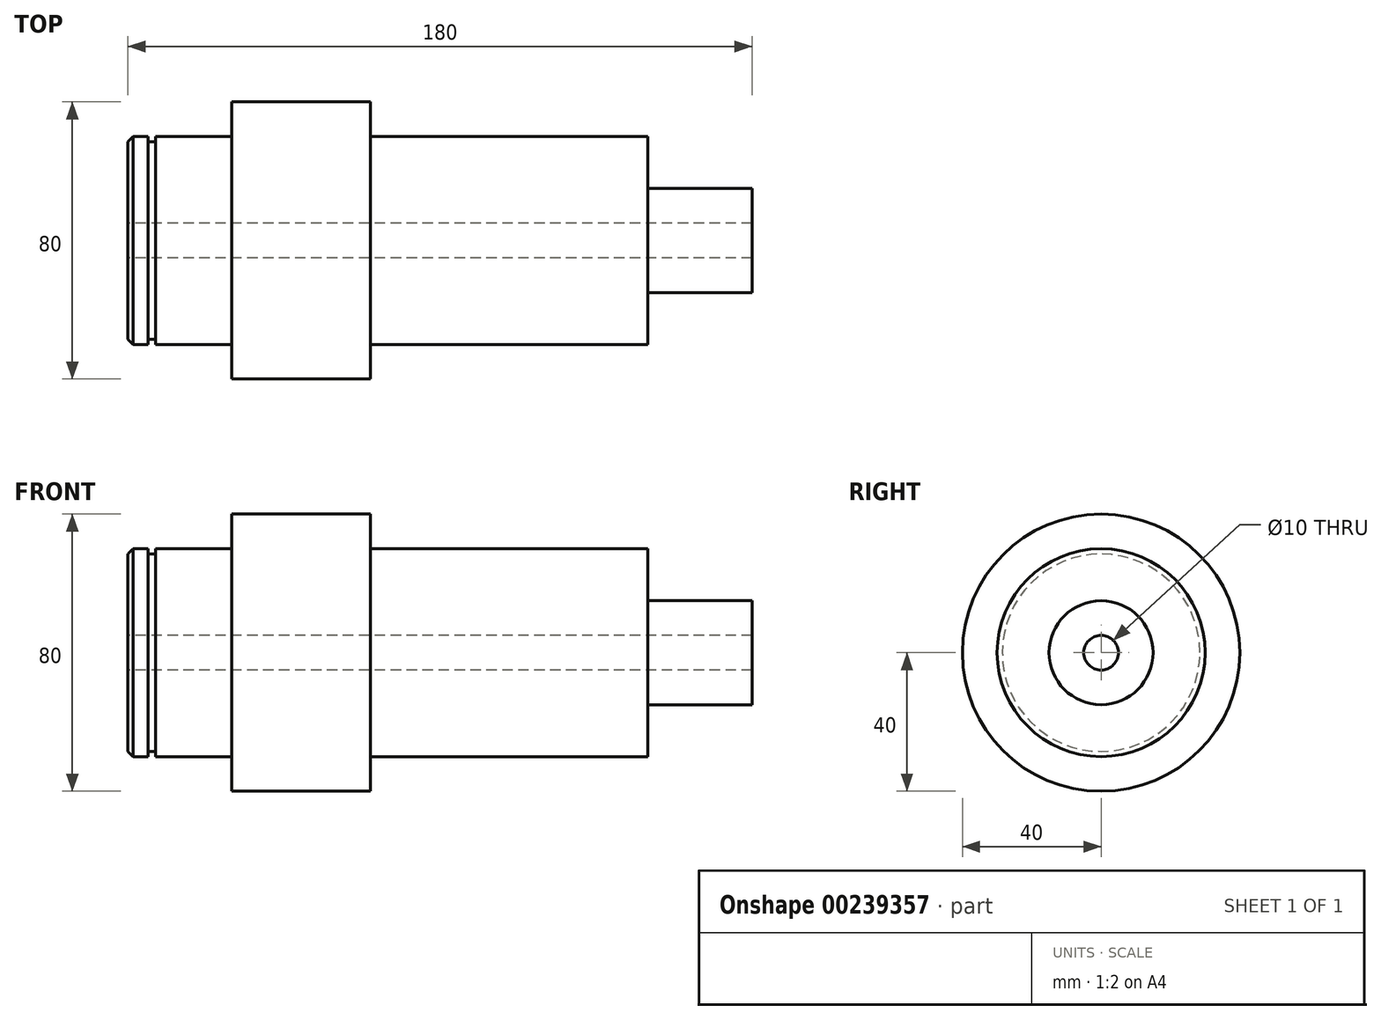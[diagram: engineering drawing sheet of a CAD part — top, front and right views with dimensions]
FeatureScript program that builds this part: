
annotation { "Feature Type Name" : "Feature", "Feature Type Description" : "" }
export const myFeature = defineFeature(function(context is Context, id is Id, definition is map)
    precondition{}
    {
        {
            var Q0;
            Q0=qCreatedBy(makeId("Front.planeOp"),FACE);
            var sketch = newSketch(context, id + "F0", { "sketchPlane" : qUnion([Q0])});
            skLineSegment(sketch, "E0", {"start": v(0, 30) * mm, "end": v(5.85, 30) * mm});
            skLineSegment(sketch, "E1", {"start": v(30, 30) * mm, "end": v(30, 40) * mm});
            skLineSegment(sketch, "E2", {"start": v(30, 40) * mm, "end": v(70, 40) * mm});
            skLineSegment(sketch, "E3", {"start": v(70, 40) * mm, "end": v(70, 30) * mm});
            skLineSegment(sketch, "E4", {"start": v(70, 30) * mm, "end": v(150, 30) * mm});
            skLineSegment(sketch, "E5", {"start": v(180, 15) * mm, "end": v(180, 5) * mm});
            skLineSegment(sketch, "E6", {"start": v(180, 5) * mm, "end": v(0, 5) * mm});
            skLineSegment(sketch, "E7", {"start": v(0, 5) * mm, "end": v(0, 30) * mm});
            skLineSegment(sketch, "E8", {"start": v(5.85, 30) * mm, "end": v(5.85, 28.5) * mm});
            skLineSegment(sketch, "E9", {"start": v(5.85, 28.5) * mm, "end": v(8, 28.5) * mm});
            skLineSegment(sketch, "E10", {"start": v(8, 28.5) * mm, "end": v(8, 30) * mm});
            skLineSegment(sketch, "E11.trimOffspring", {"start": v(8, 30) * mm, "end": v(30, 30) * mm});
            skLineSegment(sketch, "E12", {"start": v(0, 0) * mm, "end": v(148.21, 0) * mm, "construction": true});
            skLineSegment(sketch, "E13", {"start": v(150, 15) * mm, "end": v(180, 15) * mm});
            skLineSegment(sketch, "E14", {"start": v(150, 15) * mm, "end": v(150, 30) * mm});
            skSolve(sketch);
        }
        {
            var Q0;
            Q0 = qSketchRegion(id + "F0", true);
            var Q1;
            Q1=sQuery(id+"F0.wireOp",EDGE,"E12");
            revolve(context, id + "F1", {"entities" : qUnion([Q0]), "axis" : qUnion([Q1]), "revolveType" : RevolveType.FULL});
        }
        {
            var Q0;
            Q0=makeQuery(id+"F1.opRevolve","SWEPT_EDGE",EDGE,{"disambiguationData":[OSD([sQuery(id+"F0.wireOp",EDGE,"E0"),sQuery(id+"F0.wireOp",EDGE,"E7")])]});
            chamfer(context, id + "F2", {"entities" : qUnion([Q0]), "width" : 1.5 * mm, "tangentPropagation" : true});
        }
    });
